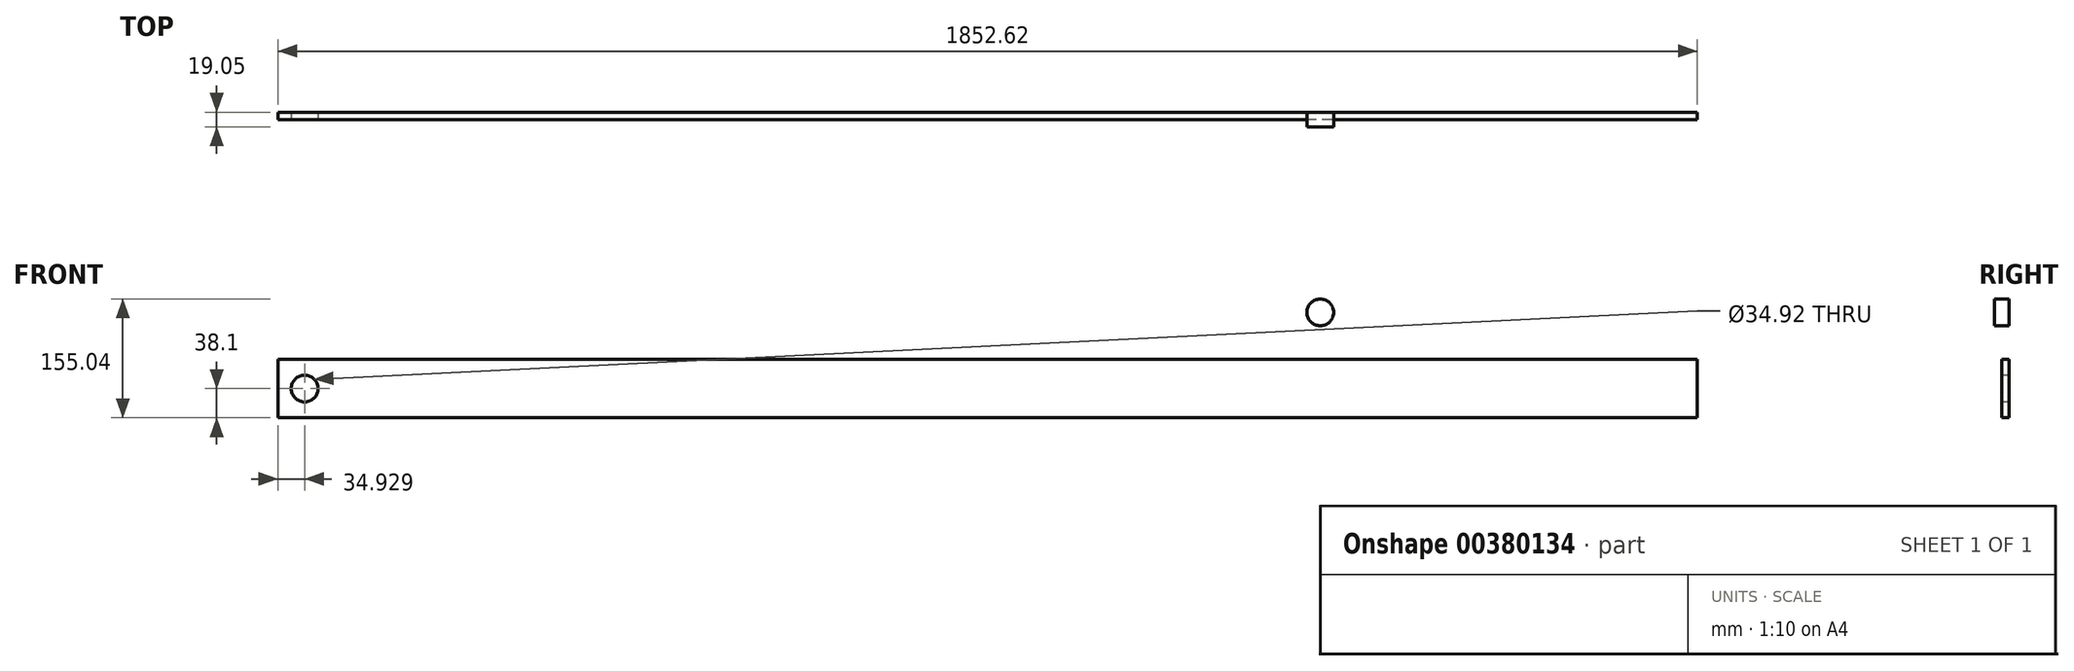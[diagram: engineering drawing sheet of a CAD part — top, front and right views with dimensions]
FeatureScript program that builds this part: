
annotation { "Feature Type Name" : "Feature", "Feature Type Description" : "" }
export const myFeature = defineFeature(function(context is Context, id is Id, definition is map)
    precondition{}
    {
        {
            var Q0;
            Q0=qCreatedBy(makeId("Front.planeOp"),FACE);
            var sketch = newSketch(context, id + "F0", { "sketchPlane" : qUnion([Q0])});
            skLineSegment(sketch, "E0.bottom", {"start": v(477.04, 12.77) * mm, "end": v(-477.04, 12.77) * mm});
            skLineSegment(sketch, "E0.top", {"start": v(477.04, 88.97) * mm, "end": v(-477.04, 88.97) * mm});
            skLineSegment(sketch, "E0.left", {"start": v(477.04, 12.77) * mm, "end": v(477.04, 88.97) * mm});
            skLineSegment(sketch, "E0.right", {"start": v(-477.04, 12.77) * mm, "end": v(-477.04, 88.97) * mm});
            skPoint(sketch, "E0.middle", {"position": v(0, 50.87) * mm});
            skSolve(sketch);
        }
        {
            var Q0;
            Q0=qCreatedBy(makeId("Front.planeOp"),FACE);
            var sketch = newSketch(context, id + "F1", { "sketchPlane" : qUnion([Q0])});
            skLineSegment(sketch, "E1.bottom", {"start": v(926.3, -86.71) * mm, "end": v(-926.3, -86.71) * mm});
            skLineSegment(sketch, "E1.top", {"start": v(926.3, -10.51) * mm, "end": v(-926.3, -10.51) * mm});
            skLineSegment(sketch, "E1.left", {"start": v(926.3, -86.71) * mm, "end": v(926.3, -10.51) * mm});
            skLineSegment(sketch, "E1.right", {"start": v(-926.3, -86.71) * mm, "end": v(-926.3, -10.51) * mm});
            skPoint(sketch, "E1.middle", {"position": v(0, -48.61) * mm});
            skSolve(sketch);
        }
        {
            var Q0;
            Q0=makeQuery(id+"F0.imprint","IMPRINT",FACE,{"disambiguationData":[TD([[makeQuery(id+"F0.imprint","IMPRINT",EDGE,{"derivedFrom":sQuery(id+"F0.wireOp",EDGE,"E0.bottom")}),-1.0]])]});
            extrude(context, id + "F2", {"entities" : qUnion([Q0]), "depth" : 19.05 * mm});
        }
        {
            var Q0;
            Q0=makeQuery(id+"F1.imprint","IMPRINT",FACE,{"disambiguationData":[TD([[makeQuery(id+"F1.imprint","IMPRINT",EDGE,{"derivedFrom":sQuery(id+"F1.wireOp",EDGE,"E1.bottom")}),-1.0]])]});
            extrude(context, id + "F3", {"entities" : qUnion([Q0]), "depth" : 9.52 * mm});
        }
        {
            var Q0;
            Q0=makeQuery(id+"F2.opExtrude","CAP_FACE",FACE,{"disambiguationData":[OSD([sQuery(id+"F0.wireOp",EDGE,"E0.bottom"),sQuery(id+"F0.wireOp",EDGE,"E0.top"),sQuery(id+"F0.wireOp",EDGE,"E0.left"),sQuery(id+"F0.wireOp",EDGE,"E0.right")])],"isStart":false});
            var sketch = newSketch(context, id + "F4", { "sketchPlane" : qUnion([Q0])});
            skCircle(sketch, "E2", {"center": v(-434.18, 50.87) * mm, "radius": 17.46 * mm});
            skPoint(sketch, "E2.centerSnap0", {"position": v(-477.04, 50.87) * mm});
            skCircle(sketch, "E3", {"center": v(-891.38, -48.61) * mm, "radius": 17.46 * mm});
            skCircle(sketch, "E4.MirrorC", {"center": v(434.18, 50.87) * mm, "radius": 17.46 * mm});
            skCircle(sketch, "E5.MirrorC", {"center": v(891.38, -48.61) * mm, "radius": 17.46 * mm});
            skSolve(sketch);
        }
        {
            var Q0;
            Q0=makeQuery(id+"F4.imprint","IMPRINT",FACE,{"disambiguationData":[TD([[makeQuery(id+"F4.imprint","IMPRINT",EDGE,{"derivedFrom":sQuery(id+"F4.wireOp",EDGE,"E2")}),1.0]])]});
            var Q1;
            Q1=makeQuery(id+"F4.imprint","IMPRINT",FACE,{"disambiguationData":[TD([[makeQuery(id+"F4.imprint","IMPRINT",EDGE,{"derivedFrom":sQuery(id+"F4.wireOp",EDGE,"E4.MirrorC")}),-1.0]])]});
            var Q2;
            Q2=makeQuery(id+"F4.imprint","IMPRINT",FACE,{"disambiguationData":[TD([[makeQuery(id+"F4.imprint","IMPRINT",EDGE,{"derivedFrom":sQuery(id+"F4.wireOp",EDGE,"E5.MirrorC")}),-1.0]])]});
            var Q3;
            Q3=makeQuery(id+"F4.imprint","IMPRINT",FACE,{"disambiguationData":[TD([[makeQuery(id+"F4.imprint","IMPRINT",EDGE,{"derivedFrom":sQuery(id+"F4.wireOp",EDGE,"E3")}),1.0]])]});
            extrude(context, id + "F5", {"entities" : qUnion([Q0, Q1, Q2, Q3]), "operationType" : NewBodyOperationType.REMOVE, "endBound" : BoundingType.THROUGH_ALL, "oppositeDirection" : true, "depth" : 25.4 * mm});
        }
    });
